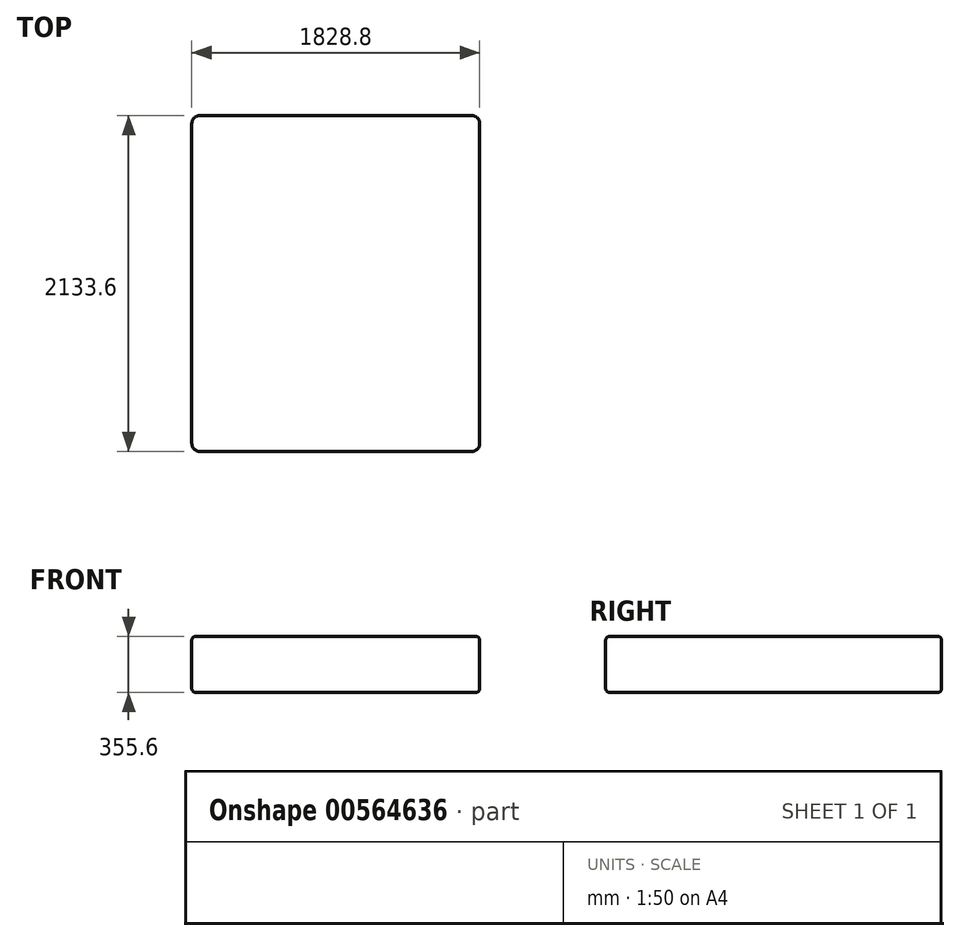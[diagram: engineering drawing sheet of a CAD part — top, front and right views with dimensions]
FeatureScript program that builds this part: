
annotation { "Feature Type Name" : "Feature", "Feature Type Description" : "" }
export const myFeature = defineFeature(function(context is Context, id is Id, definition is map)
    precondition{}
    {
        {
            var Q0;
            Q0=qCreatedBy(makeId("Top.planeOp"),FACE);
            var sketch = newSketch(context, id + "F0", { "sketchPlane" : qUnion([Q0])});
            skLineSegment(sketch, "E0.bottom", {"start": v(-914.4, 1066.8) * mm, "end": v(914.4, 1066.8) * mm});
            skLineSegment(sketch, "E0.top", {"start": v(-914.4, -1066.8) * mm, "end": v(914.4, -1066.8) * mm});
            skLineSegment(sketch, "E0.left", {"start": v(-914.4, 1066.8) * mm, "end": v(-914.4, -1066.8) * mm});
            skLineSegment(sketch, "E0.right", {"start": v(914.4, 1066.8) * mm, "end": v(914.4, -1066.8) * mm});
            skPoint(sketch, "E0.middle", {"position": v(0, 0) * mm});
            skSolve(sketch);
        }
        {
            var Q0;
            Q0=makeQuery(id+"F0.imprint","IMPRINT",FACE,{"disambiguationData":[TD([[makeQuery(id+"F0.imprint","IMPRINT",EDGE,{"derivedFrom":sQuery(id+"F0.wireOp",EDGE,"E0.bottom")}),-1.0]])]});
            extrude(context, id + "F1", {"entities" : qUnion([Q0]), "depth" : 355.6 * mm, "offsetDistance" : 25.4 * mm});
        }
        {
            var Q0;
            Q0=makeQuery(id+"F1.opExtrude","SWEPT_EDGE",EDGE,{"disambiguationData":[OSD([sQuery(id+"F0.wireOp",EDGE,"E0.bottom"),sQuery(id+"F0.wireOp",EDGE,"E0.left")])]});
            var Q1;
            Q1=makeQuery(id+"F1.opExtrude","SWEPT_EDGE",EDGE,{"disambiguationData":[OSD([sQuery(id+"F0.wireOp",EDGE,"E0.top"),sQuery(id+"F0.wireOp",EDGE,"E0.left")])]});
            var Q2;
            Q2=makeQuery(id+"F1.opExtrude","SWEPT_EDGE",EDGE,{"disambiguationData":[OSD([sQuery(id+"F0.wireOp",EDGE,"E0.bottom"),sQuery(id+"F0.wireOp",EDGE,"E0.right")])]});
            var Q3;
            Q3=makeQuery(id+"F1.opExtrude","SWEPT_EDGE",EDGE,{"disambiguationData":[OSD([sQuery(id+"F0.wireOp",EDGE,"E0.top"),sQuery(id+"F0.wireOp",EDGE,"E0.right")])]});
            fillet(context, id + "F2", {"entities" : qUnion([Q0, Q1, Q2, Q3]), "radius" : 50.8 * mm, "tangentPropagation" : true, "allowEdgeOverflow" : false});
        }
        {
            var Q0;
            Q0=makeQuery(id+"F1.opExtrude","CAP_EDGE",EDGE,{"disambiguationData":[OSD([sQuery(id+"F0.wireOp",EDGE,"E0.top")])],"isStart":false});
            var Q1;
            Q1=makeQuery(id+"F1.opExtrude","CAP_EDGE",EDGE,{"disambiguationData":[OSD([sQuery(id+"F0.wireOp",EDGE,"E0.top")])],"isStart":true});
            fillet(context, id + "F3", {"entities" : qUnion([Q0, Q1]), "radius" : 25.4 * mm, "tangentPropagation" : true, "allowEdgeOverflow" : false});
        }
    });
